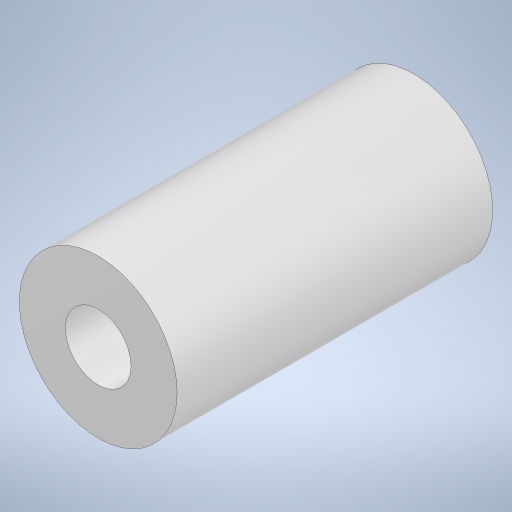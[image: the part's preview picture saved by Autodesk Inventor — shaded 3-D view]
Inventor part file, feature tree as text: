
AUTODESK INVENTOR PART (.ipt)
format: ipt  version: 2023 (Build 270158000, 158)  size: 205,312 bytes
history: native  units: mm
features: extrude x1, sketch x1
ambient origin geometry x8: Origin, YZ Plane, XZ Plane, XY Plane, X Axis, Y Axis, Z Axis, Center Point
bodies: Solid1 (feature_tree)
feature tree (2):
  extrude  "Extrusion1"  Depth=12.0mm
  sketch  "Sketch1"  dims[d0=2.5mm d1=6.0mm d2=12.0mm d3=0.0mm]
